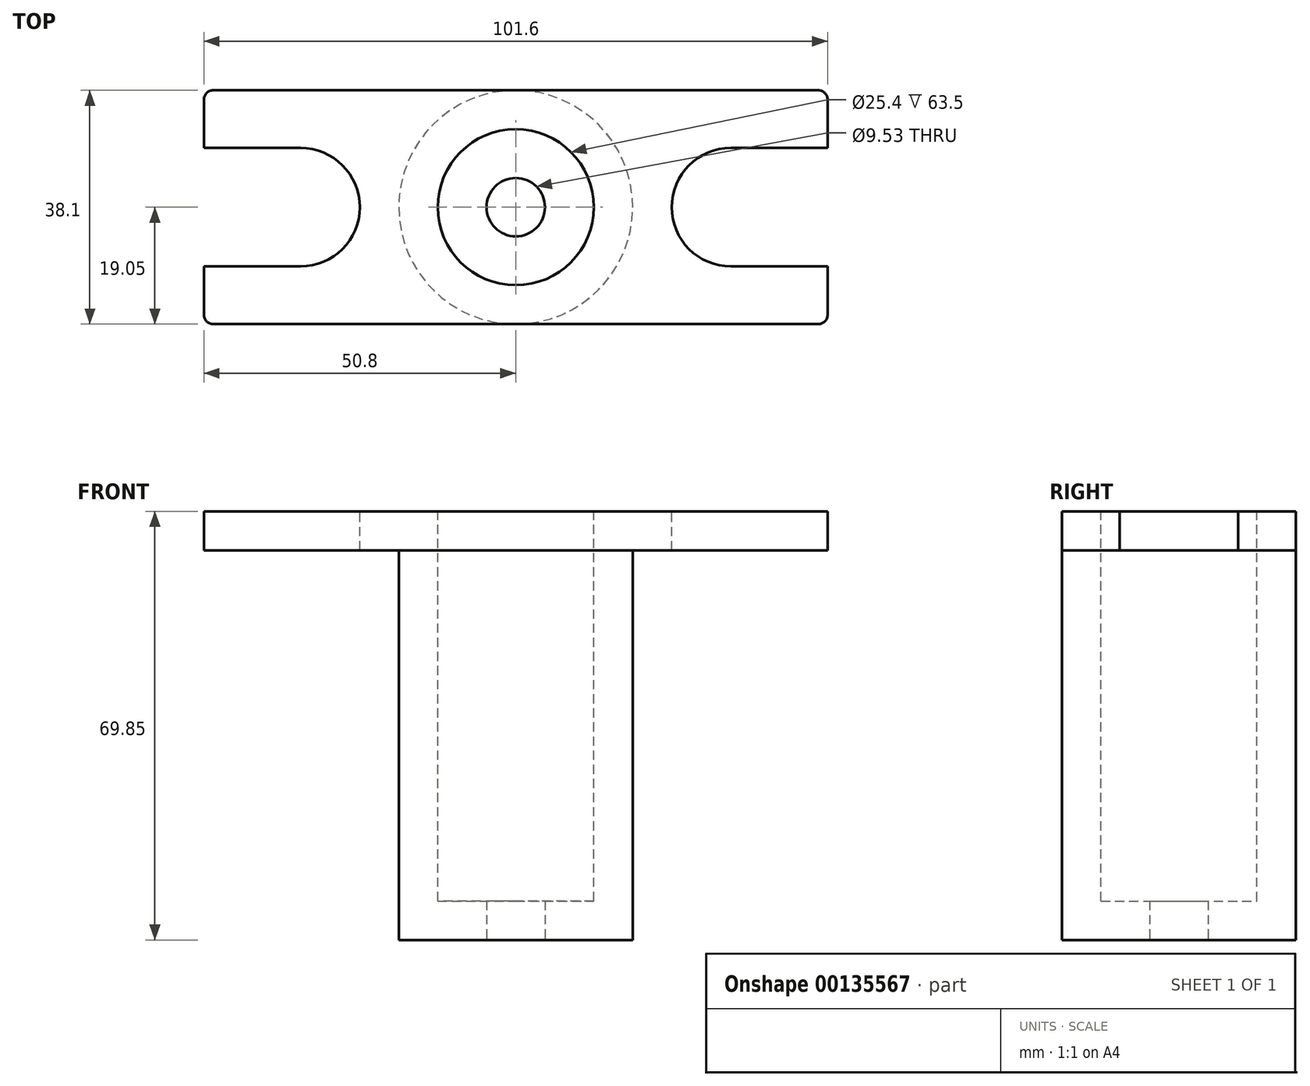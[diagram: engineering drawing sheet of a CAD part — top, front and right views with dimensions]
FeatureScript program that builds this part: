
annotation { "Feature Type Name" : "Feature", "Feature Type Description" : "" }
export const myFeature = defineFeature(function(context is Context, id is Id, definition is map)
    precondition{}
    {
        {
            var Q0;
            Q0=qCreatedBy(makeId("Top.planeOp"),FACE);
            var sketch = newSketch(context, id + "F0", { "sketchPlane" : qUnion([Q0])});
            skCircle(sketch, "E0", {"center": v(0, 0) * mm, "radius": 19.05 * mm});
            skSolve(sketch);
        }
        {
            var Q0;
            Q0 = qSketchRegion(id + "F0", true);
            extrude(context, id + "F1", {"entities" : qUnion([Q0]), "depth" : 69.85 * mm});
        }
        {
            var Q0;
            Q0=makeQuery(id+"F1.opExtrude","CAP_FACE",FACE,{"disambiguationData":[OSD([sQuery(id+"F0.wireOp",EDGE,"E0")])],"isStart":false});
            var sketch = newSketch(context, id + "F2", { "sketchPlane" : qUnion([Q0])});
            skCircle(sketch, "E1", {"center": v(0, 0) * mm, "radius": 12.7 * mm});
            skSolve(sketch);
        }
        {
            var Q0;
            Q0 = qSketchRegion(id + "F2", true);
            extrude(context, id + "F3", {"entities" : qUnion([Q0]), "operationType" : NewBodyOperationType.REMOVE, "oppositeDirection" : true, "depth" : 63.5 * mm});
        }
        {
            var Q0;
            Q0=makeQuery(id+"F1.opExtrude","CAP_FACE",FACE,{"disambiguationData":[OSD([sQuery(id+"F0.wireOp",EDGE,"E0")])],"isStart":true});
            var sketch = newSketch(context, id + "F4", { "sketchPlane" : qUnion([Q0])});
            skCircle(sketch, "E2", {"center": v(0, 0) * mm, "radius": 4.76 * mm});
            skSolve(sketch);
        }
        {
            var Q0;
            Q0 = qSketchRegion(id + "F4", true);
            extrude(context, id + "F5", {"entities" : qUnion([Q0]), "operationType" : NewBodyOperationType.REMOVE, "endBound" : BoundingType.THROUGH_ALL, "oppositeDirection" : true, "depth" : 25.4 * mm});
        }
        {
            var Q0;
            Q0=makeQuery(id+"F1.opExtrude","CAP_FACE",FACE,{"disambiguationData":[OSD([sQuery(id+"F0.wireOp",EDGE,"E0")])],"isStart":false});
            var sketch = newSketch(context, id + "F6", { "sketchPlane" : qUnion([Q0])});
            skLineSegment(sketch, "E3.bottom", {"start": v(17.53, -50.8) * mm, "end": v(-17.53, -50.8) * mm});
            skLineSegment(sketch, "E3.top", {"start": v(17.53, 50.8) * mm, "end": v(-17.53, 50.8) * mm});
            skLineSegment(sketch, "E3.left", {"start": v(19.05, -49.28) * mm, "end": v(19.05, 49.28) * mm});
            skLineSegment(sketch, "E3.right", {"start": v(-19.05, -49.28) * mm, "end": v(-19.05, 49.28) * mm});
            skPoint(sketch, "E4.visualSharp", {"position": v(19.05, -50.8) * mm});
            skArc(sketch, "E4.filletArc", {"start": v(17.53, -50.8) * mm, "mid": v(18.6, -50.35) * mm, "end": v(19.05, -49.28) * mm});
            skPoint(sketch, "E5.visualSharp", {"position": v(-19.05, -50.8) * mm});
            skArc(sketch, "E5.filletArc", {"start": v(-19.05, -49.28) * mm, "mid": v(-18.6, -50.35) * mm, "end": v(-17.53, -50.8) * mm});
            skPoint(sketch, "E6.visualSharp", {"position": v(19.05, 50.8) * mm});
            skArc(sketch, "E6.filletArc", {"start": v(19.05, 49.28) * mm, "mid": v(18.6, 50.35) * mm, "end": v(17.53, 50.8) * mm});
            skPoint(sketch, "E7.visualSharp", {"position": v(-19.05, 50.8) * mm});
            skArc(sketch, "E7.filletArc", {"start": v(-17.53, 50.8) * mm, "mid": v(-18.6, 50.35) * mm, "end": v(-19.05, 49.28) * mm});
            skArc(sketch, "E8", {"start": v(-9.65, 35.05) * mm, "mid": v(0, 25.4) * mm, "end": v(9.65, 35.05) * mm});
            skLineSegment(sketch, "E9", {"start": v(24.8, 0) * mm, "end": v(-28.36, 0) * mm, "construction": true});
            skLineSegment(sketch, "E10", {"start": v(9.65, 35.05) * mm, "end": v(9.65, 50.8) * mm});
            skLineSegment(sketch, "E11", {"start": v(-9.65, 35.05) * mm, "end": v(-9.65, 50.8) * mm});
            skLineSegment(sketch, "E12", {"start": v(9.65, 50.8) * mm, "end": v(-9.65, 50.8) * mm});
            skArc(sketch, "E13.MirrorCS", {"start": v(-9.65, -35.05) * mm, "mid": v(0, -25.4) * mm, "end": v(9.65, -35.05) * mm});
            skLineSegment(sketch, "E14.MirrorCS", {"start": v(9.65, -35.05) * mm, "end": v(9.65, -50.8) * mm});
            skLineSegment(sketch, "E15.MirrorCS", {"start": v(-9.65, -35.05) * mm, "end": v(-9.65, -50.8) * mm});
            skLineSegment(sketch, "E16", {"start": v(9.65, -50.8) * mm, "end": v(-9.65, -50.8) * mm});
            skSolve(sketch);
        }
        {
            var Q0;
            {var subQ9=sQuery(id+"F6.wireOp",EDGE,"E4.filletArc");Q0=makeQuery(id+"F6.imprint","IMPRINT",FACE,{"disambiguationData":[TD([[makeQuery(id+"F6.imprint","IMPRINT",EDGE,{"derivedFrom":subQ9}),1.0]])]});}
            var Q1;
            {var subQ0=sQuery(id+"F6.wireOp",EDGE,"E6.filletArc");Q1=makeQuery(id+"F6.imprint","IMPRINT",FACE,{"disambiguationData":[TD([[makeQuery(id+"F6.imprint","IMPRINT",EDGE,{"derivedFrom":subQ0}),1.0]])]});}
            extrude(context, id + "F7", {"entities" : qUnion([Q0, Q1]), "operationType" : NewBodyOperationType.ADD, "oppositeDirection" : true, "depth" : 6.35 * mm});
        }
        {
            var Q0;
            Q0=makeQuery(id+"F1.opExtrude","SWEPT_BODY",BODY,{"disambiguationData":[OSD([sQuery(id+"F0.wireOp",EDGE,"E0")])]});
            var Q1;
            Q1=makeQuery(id+"F3.boolean.opBoolean","COPY",FACE,{"derivedFrom":makeQuery(id+"F3.opExtrude","SWEPT_FACE",FACE,{"disambiguationData":[OSD([sQuery(id+"F2.wireOp",EDGE,"E1")])]})});
            transform(context, id + "F8", {"entities" : qUnion([Q0]), "transformType" : TransformType.ROTATION, "transformAxis" : qUnion([Q1]), "angle" : 90 * degree, "makeCopy" : false});
        }
    });
